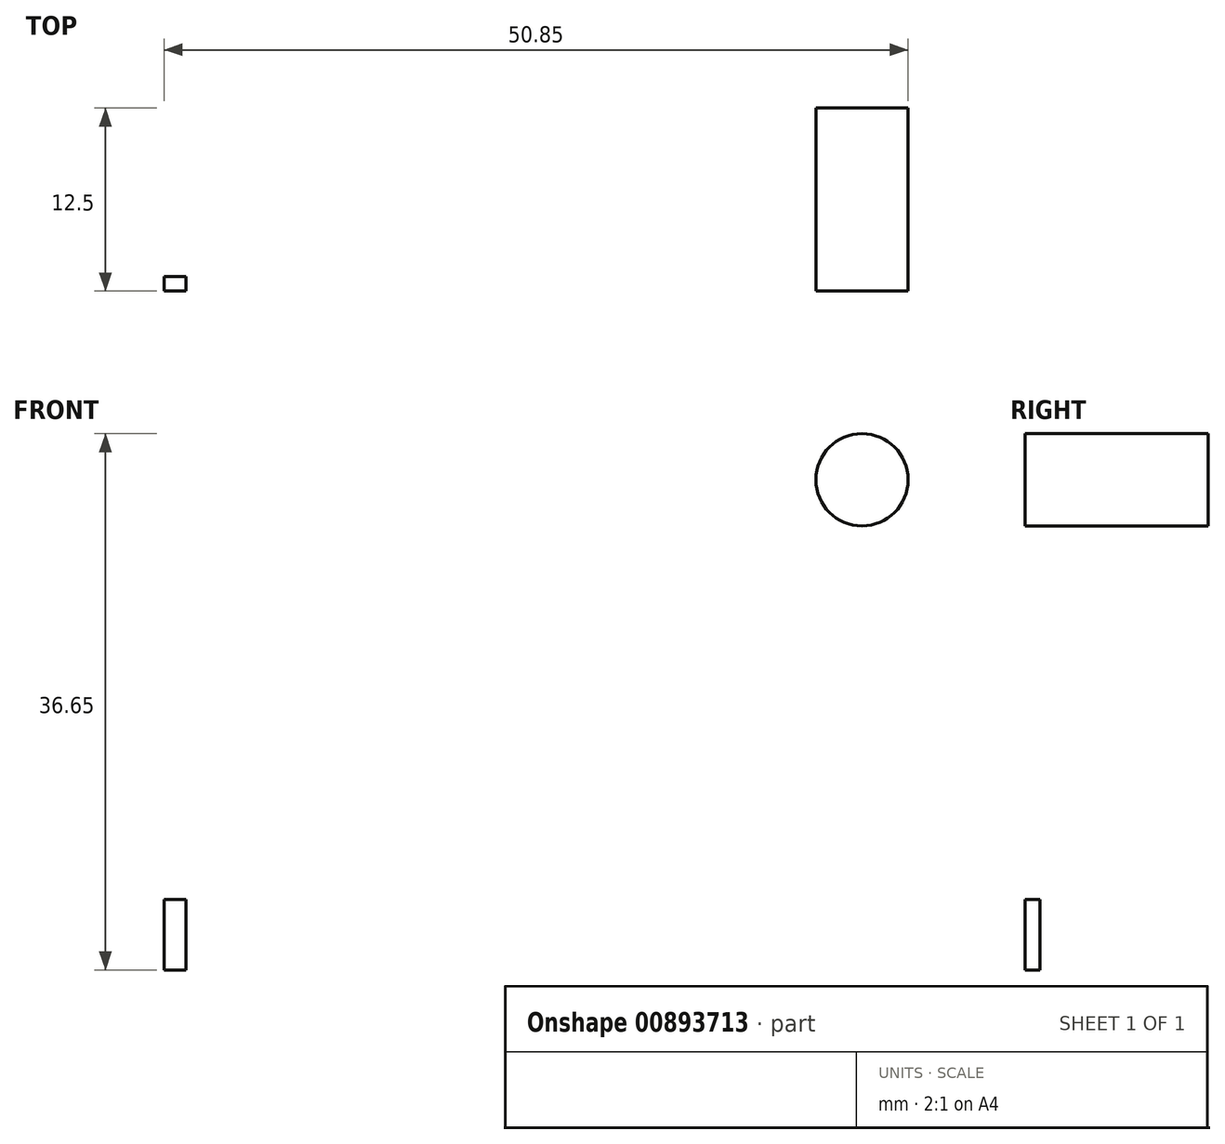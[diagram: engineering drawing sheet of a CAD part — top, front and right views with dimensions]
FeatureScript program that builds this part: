
annotation { "Feature Type Name" : "Feature", "Feature Type Description" : "" }
export const myFeature = defineFeature(function(context is Context, id is Id, definition is map)
    precondition{}
    {
        {
            var Q0;
            Q0=qCreatedBy(makeId("Front.planeOp"),FACE);
            var sketch = newSketch(context, id + "F0", { "sketchPlane" : qUnion([Q0])});
            skLineSegment(sketch, "E0.bottom", {"start": v(28, -33.5) * mm, "end": v(-28, -33.5) * mm});
            skLineSegment(sketch, "E0.top", {"start": v(28, 33.5) * mm, "end": v(-28, 33.5) * mm});
            skLineSegment(sketch, "E0.left", {"start": v(28, -33.5) * mm, "end": v(28, 33.5) * mm});
            skLineSegment(sketch, "E0.right", {"start": v(-28, -33.5) * mm, "end": v(-28, 33.5) * mm});
            skPoint(sketch, "E0.middle", {"position": v(0, 0) * mm});
            skLineSegment(sketch, "E1", {"start": v(-28, 33.5) * mm, "end": v(-26.5, 33.5) * mm});
            skLineSegment(sketch, "E2", {"start": v(-26.5, 33.5) * mm, "end": v(-26.5, 28.7) * mm});
            skLineSegment(sketch, "E3", {"start": v(-26.5, 28.7) * mm, "end": v(-28, 28.7) * mm});
            skLineSegment(sketch, "E4", {"start": v(-28, -33.5) * mm, "end": v(-26.5, -33.5) * mm});
            skLineSegment(sketch, "E5", {"start": v(-26.5, -33.5) * mm, "end": v(-26.5, -28.7) * mm});
            skLineSegment(sketch, "E6", {"start": v(-26.5, -28.7) * mm, "end": v(-28, -28.7) * mm});
            skCircle(sketch, "E7", {"center": v(19.7, 0) * mm, "radius": 3.15 * mm});
            skSolve(sketch);
        }
        {
            var Q0;
            Q0=makeQuery(id+"F0.imprint","IMPRINT",FACE,{"disambiguationData":[TD([[makeQuery(id+"F0.imprint","IMPRINT",EDGE,{"derivedFrom":sQuery(id+"F0.wireOp",EDGE,"E7")}),1.0]])]});
            var Q1;
            Q1=sQuery(id+"F0.wireOp",EDGE,"E7");
            extrude(context, id + "F1", {"entities" : qUnion([Q0]), "surfaceEntities" : qUnion([Q1]), "oppositeDirection" : true, "depth" : 12.5 * mm, "offsetDistance" : 25.4 * mm});
        }
        {
            var Q0;
            Q0=makeQuery(id+"F0.imprint","IMPRINT",FACE,{"disambiguationData":[TD([[makeQuery(id+"F0.imprint","IMPRINT",EDGE,{"derivedFrom":sQuery(id+"F0.wireOp",EDGE,"E0.bottom")}),-1.0]])]});
            extrude(context, id + "F2", {"entities" : qUnion([Q0]), "oppositeDirection" : true, "depth" : 1 * mm, "offsetDistance" : 25.4 * mm});
        }
    });
